# Revit family: 302-BFD-LIH-DSD-PL-___ (LOD400)
name_source: partatom
category: Fire Alarm Devices
revit_build: Autodesk Revit 2018 (Build: 20170223_1515(x64)
units: mm (PartAtom-declared; Revit-internal decimal feet)

## family parameters
Cut with Voids When Loaded = No
Host = Face
Maintain Annotation Orientation = No
OmniClass Number = 23.29.29.13.13
OmniClass Title = Heat Detectors
Part Type = Normal
Room Calculation Point = No
Round Connector Dimension = Use Diameter
Shared = No

## types (1)
- 302-BFD-LIH-DSD-PL-___ (LOD400)
    D = 120 mm  [stored 0.393701 ft]
    DSD.BFD.Height = 0 mm  [stored 0 ft]
    DSD.BFD.Length = 0 mm  [stored 0 ft]
    DSD.BFD.Width = 0 mm  [stored 0 ft]
    DSD.Com.CAT Code = BFD
    Default Elevation = 1219 mm
    L = 200 mm  [stored 0.656168 ft]
    W = 80 mm  [stored 0.262467 ft]

note: [stored X ft] marks values corroborated as IEEE doubles in the binary element streams (Revit-internal decimal feet)

## geometry (parser evidence)
native form markers: Blend x2, Sweep x6
no freeform markers — native parametric forms only
